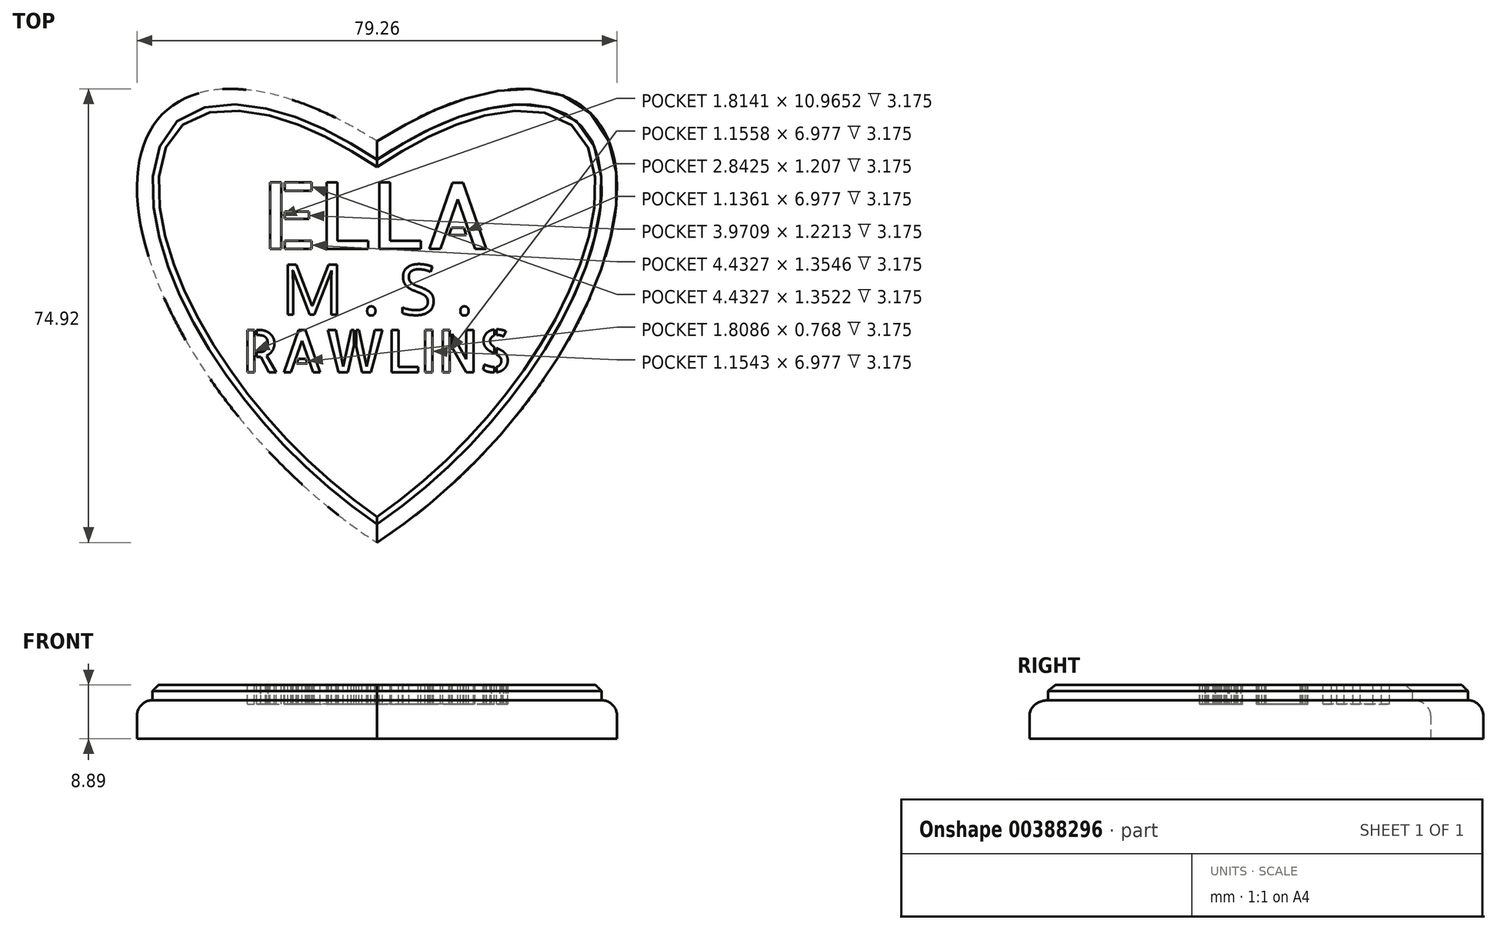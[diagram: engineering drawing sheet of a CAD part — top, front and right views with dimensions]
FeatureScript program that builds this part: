
annotation { "Feature Type Name" : "Feature", "Feature Type Description" : "" }
export const myFeature = defineFeature(function(context is Context, id is Id, definition is map)
    precondition{}
    {
        {
            var Q0;
            Q0=qCreatedBy(makeId("Top.planeOp"),FACE);
            var sketch = newSketch(context, id + "F0", { "sketchPlane" : qUnion([Q0])});
            skLineSegment(sketch, "E0.bottom", {"start": v(-34.92, 38.1) * mm, "end": v(34.93, 38.1) * mm});
            skLineSegment(sketch, "E0.top", {"start": v(-34.93, -38.1) * mm, "end": v(34.92, -38.1) * mm});
            skLineSegment(sketch, "E0.left", {"start": v(-34.92, 38.1) * mm, "end": v(-34.93, -38.1) * mm});
            skLineSegment(sketch, "E0.right", {"start": v(34.93, 38.1) * mm, "end": v(34.92, -38.1) * mm});
            skPoint(sketch, "E0.middle", {"position": v(0, 0) * mm});
            skEllipse(sketch, "E1", {"center": v(0, 0) * mm, "majorRadius": 51.69 * mm, "minorRadius": 25.4 * mm, "majorAxis": v(-0.68, 0.74)});
            skEllipse(sketch, "E2", {"center": v(0, 0) * mm, "majorRadius": 51.69 * mm, "minorRadius": 25.4 * mm, "majorAxis": v(0.68, 0.74)});
            skSolve(sketch);
        }
        {
            var Q0;
            {var subQ0=sQuery(id+"F0.wireOp",EDGE,"E2");var subQ1=sQuery(id+"F0.wireOp",EDGE,"E1");var subQ2=makeQuery(id+"F0.imprint","INTERSECT",VERTEX,{"disambiguationData":[OD(0.0)],"derivedFrom":[subQ1,subQ0]});Q0=makeQuery(id+"F0.imprint","IMPRINT",FACE,{"disambiguationData":[TD([[makeQuery(id+"F0.imprint","IMPRINT",EDGE,{"disambiguationData":[TD([[subQ2,-1.0]])],"derivedFrom":subQ1}),1.0]])]});}
            var Q1;
            {var subQ0=sQuery(id+"F0.wireOp",EDGE,"E2");var subQ3=sQuery(id+"F0.wireOp",EDGE,"E1");var subQ5=makeQuery(id+"F0.imprint","INTERSECT",VERTEX,{"disambiguationData":[OD(2.0)],"derivedFrom":[subQ3,subQ0]});Q1=makeQuery(id+"F0.imprint","IMPRINT",FACE,{"disambiguationData":[TD([[makeQuery(id+"F0.imprint","IMPRINT",EDGE,{"disambiguationData":[TD([[subQ5,-1.0]])],"derivedFrom":subQ3}),-1.0]])]});}
            var Q2;
            {var subQ0=sQuery(id+"F0.wireOp",EDGE,"E1");var subQ1=sQuery(id+"F0.wireOp",EDGE,"E0.left");var subQ2=makeQuery(id+"F0.imprint","INTERSECT",VERTEX,{"derivedFrom":[subQ1,subQ0]});Q2=makeQuery(id+"F0.imprint","IMPRINT",FACE,{"disambiguationData":[TD([[makeQuery(id+"F0.imprint","IMPRINT",EDGE,{"disambiguationData":[TD([[subQ2,-1.0]])],"derivedFrom":subQ0}),1.0]])]});}
            var Q3;
            {var subQ0=sQuery(id+"F0.wireOp",EDGE,"E1");var subQ1=sQuery(id+"F0.wireOp",EDGE,"E0.left");var subQ3=makeQuery(id+"F0.imprint","INTERSECT",VERTEX,{"derivedFrom":[subQ1,subQ0]});Q3=makeQuery(id+"F0.imprint","IMPRINT",FACE,{"disambiguationData":[TD([[makeQuery(id+"F0.imprint","IMPRINT",EDGE,{"disambiguationData":[TD([[subQ3,1.0]])],"derivedFrom":subQ1}),-1.0]])]});}
            var Q4;
            {var subQ0=sQuery(id+"F0.wireOp",EDGE,"E2");var subQ1=sQuery(id+"F0.wireOp",EDGE,"E0.right");var subQ3=makeQuery(id+"F0.imprint","INTERSECT",VERTEX,{"derivedFrom":[subQ1,subQ0]});Q4=makeQuery(id+"F0.imprint","IMPRINT",FACE,{"disambiguationData":[TD([[makeQuery(id+"F0.imprint","IMPRINT",EDGE,{"disambiguationData":[TD([[subQ3,1.0]])],"derivedFrom":subQ1}),1.0]])]});}
            var Q5;
            {var subQ0=sQuery(id+"F0.wireOp",EDGE,"E1");var subQ1=sQuery(id+"F0.wireOp",EDGE,"E0.bottom");var subQ3=makeQuery(id+"F0.imprint","INTERSECT",VERTEX,{"derivedFrom":[subQ1,subQ0]});Q5=makeQuery(id+"F0.imprint","IMPRINT",FACE,{"disambiguationData":[TD([[makeQuery(id+"F0.imprint","IMPRINT",EDGE,{"disambiguationData":[TD([[subQ3,1.0]])],"derivedFrom":subQ1}),1.0]])]});}
            var Q6;
            {var subQ0=sQuery(id+"F0.wireOp",EDGE,"E2");var subQ1=sQuery(id+"F0.wireOp",EDGE,"E0.bottom");var subQ3=makeQuery(id+"F0.imprint","INTERSECT",VERTEX,{"derivedFrom":[subQ1,subQ0]});Q6=makeQuery(id+"F0.imprint","IMPRINT",FACE,{"disambiguationData":[TD([[makeQuery(id+"F0.imprint","IMPRINT",EDGE,{"disambiguationData":[TD([[subQ3,-1.0]])],"derivedFrom":subQ1}),1.0]])]});}
            extrude(context, id + "F1", {"entities" : qUnion([Q0, Q1, Q2, Q3, Q4, Q5, Q6]), "depth" : 6.35 * mm});
        }
        {
            var Q0;
            Q0=makeQuery(id+"F1.opExtrude","CAP_EDGE",EDGE,{"disambiguationData":[OSD([sQuery(id+"F0.wireOp",EDGE,"E1")])],"isStart":false});
            var Q1;
            Q1=makeQuery(id+"F1.opExtrude","CAP_EDGE",EDGE,{"disambiguationData":[OSD([sQuery(id+"F0.wireOp",EDGE,"E2")])],"isStart":false});
            fillet(context, id + "F2", {"entities" : qUnion([Q0, Q1]), "radius" : 2.54 * mm, "tangentPropagation" : true, "allowEdgeOverflow" : false});
        }
        {
            var Q0;
            Q0=makeQuery(id+"F1.opExtrude","CAP_FACE",FACE,{"disambiguationData":[OSD([sQuery(id+"F0.wireOp",EDGE,"E1"),sQuery(id+"F0.wireOp",EDGE,"E2")])],"isStart":false});
            extrude(context, id + "F3", {"entities" : qUnion([Q0]), "operationType" : NewBodyOperationType.ADD, "depth" : 2.54 * mm});
        }
        {
            var Q0;
            {var subQ0=sQuery(id+"F0.wireOp",EDGE,"E2");var subQ1=sQuery(id+"F0.wireOp",EDGE,"E1");Q0=makeQuery(id+"F3.opExtrude","CAP_EDGE",EDGE,{"disambiguationData":[OSD([subQ1,subQ0]),TDD([makeQuery(id+"F2.opFillet","BLEND_EDGE",EDGE,{"blendedFrom":[makeQuery(id+"F1.opExtrude","CAP_EDGE",EDGE,{"disambiguationData":[OSD([subQ1])],"isStart":false}),makeQuery(id+"F1.opExtrude","CAP_FACE",FACE,{"disambiguationData":[OSD([subQ1,subQ0])],"isStart":false})],"blendedInto":[makeQuery(id+"F1.opExtrude","CAP_FACE",FACE,{"disambiguationData":[OSD([subQ1,subQ0])],"isStart":false})]})])],"isStart":false});}
            var Q1;
            {var subQ0=sQuery(id+"F0.wireOp",EDGE,"E2");var subQ1=sQuery(id+"F0.wireOp",EDGE,"E1");Q1=makeQuery(id+"F3.opExtrude","CAP_EDGE",EDGE,{"disambiguationData":[OSD([subQ1,subQ0]),TDD([makeQuery(id+"F2.opFillet","BLEND_EDGE",EDGE,{"blendedFrom":[makeQuery(id+"F1.opExtrude","CAP_EDGE",EDGE,{"disambiguationData":[OSD([subQ0])],"isStart":false}),makeQuery(id+"F1.opExtrude","CAP_FACE",FACE,{"disambiguationData":[OSD([subQ1,subQ0])],"isStart":false})],"blendedInto":[makeQuery(id+"F1.opExtrude","CAP_FACE",FACE,{"disambiguationData":[OSD([subQ1,subQ0])],"isStart":false})]})])],"isStart":false});}
            chamfer(context, id + "F4", {"entities" : qUnion([Q0, Q1]), "width" : 1.02 * mm, "tangentPropagation" : true});
        }
        {
            var Q0;
            Q0=makeQuery(id+"F3.opExtrude","CAP_FACE",FACE,{"disambiguationData":[OSD([sQuery(id+"F0.wireOp",EDGE,"E1"),sQuery(id+"F0.wireOp",EDGE,"E2")])],"isStart":false});
            var sketch = newSketch(context, id + "F5", { "sketchPlane" : qUnion([Q0])});
            skText(sketch, "E3", { "text": "ELLA", "fontName": "AllertaStencil-Regular.ttf"});
            skText(sketch, "E4", { "text": "RAWLINS", "fontName": "AllertaStencil-Regular.ttf"});
            skText(sketch, "E5", { "text": "M . S .", "fontName": "OpenSans-Regular.ttf"});
            const initialGuessF5  = {"E3": [-0.01905, 0.01536, 1, 0, 0.01097], "E4": [-0.02223, -0.005, 1, 0, 0.00698], "E5": [-0.01588, 0.00452, 1, 0, 0.0083]};
            skSetInitialGuess(sketch, initialGuessF5);
            skSolve(sketch);
        }
        {
            var Q0;
            Q0=qSketchRegion(id+"F5",true);
            extrude(context, id + "F6", {"entities" : qUnion([Q0]), "operationType" : NewBodyOperationType.REMOVE, "oppositeDirection" : true, "depth" : 3.17 * mm});
        }
    });
